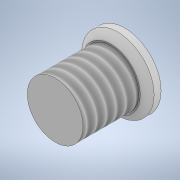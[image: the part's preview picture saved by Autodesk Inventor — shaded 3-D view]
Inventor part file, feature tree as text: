
AUTODESK INVENTOR PART (.ipt)
format: ipt  version: 2021 (Build 250183000, 183)  size: 116,736 bytes
history: native  units: mm
features: extrude x2, sketch x2, thread x1, chamfer x1
ambient origin geometry x8: Origin, YZ Plane, XZ Plane, XY Plane, X Axis, Y Axis, Z Axis, Center Point
bodies: Solid1 (feature_tree)
feature tree (6):
  extrude  "Extrusion1"  Depth=1.0mm TaperAngle=0.0deg
  extrude  "Extrusion2"  Depth=4.0mm TaperAngle=0.0deg
  thread  "Thread1"  [1 undecoded]
  chamfer  "Chamfer2"  Distance=2.0mm Angle=45.0deg
  sketch  "Sketch1"  dims[d0=5.2mm d1=1.0mm d2=0.0mm]
  sketch  "Sketch2"  dims[d3=4.0mm d4=4.0mm d5=0.0mm d6=5.0mm d7=0.0mm d22=0.5mm d23=2.0mm d24=45.0deg]
note: 1 required parameter value undecoded (feature->parameter linkage not recoverable at this tier; creation-order binding heuristic only, values carry confidence <= 0.55)
